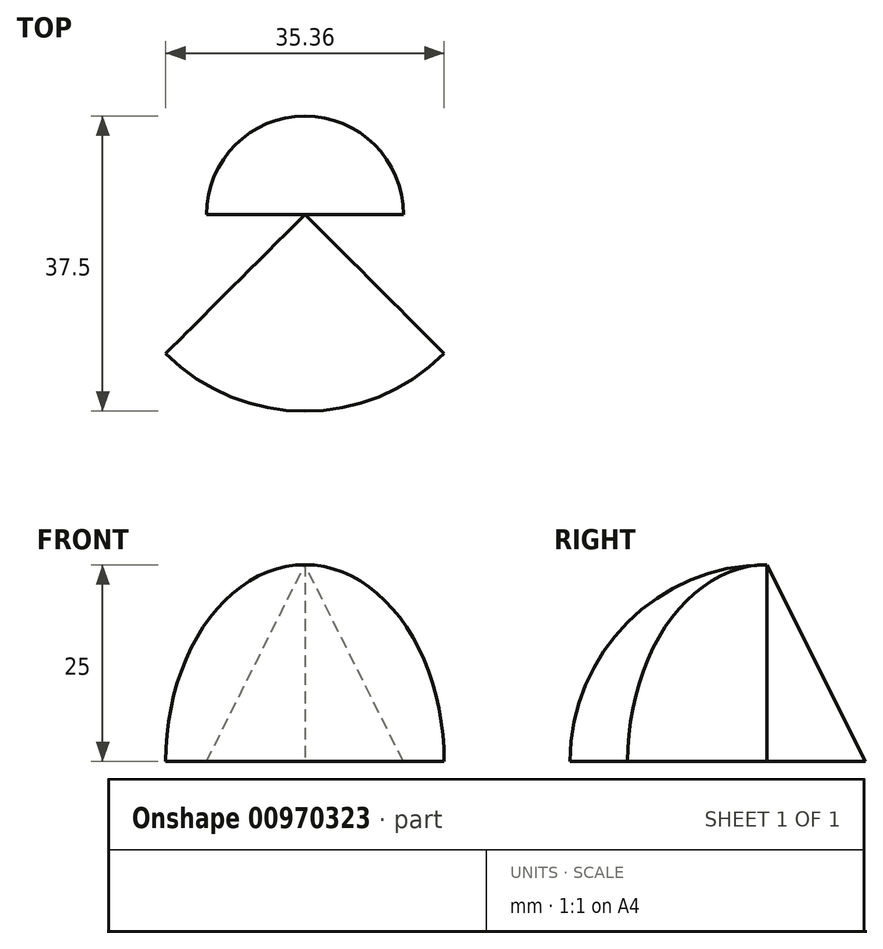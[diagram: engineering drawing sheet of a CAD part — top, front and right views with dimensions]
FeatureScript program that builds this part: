
annotation { "Feature Type Name" : "Feature", "Feature Type Description" : "" }
export const myFeature = defineFeature(function(context is Context, id is Id, definition is map)
    precondition{}
    {
        {
            var Q0;
            Q0=qCreatedBy(makeId("Front.planeOp"),FACE);
            var sketch = newSketch(context, id + "F0", { "sketchPlane" : qUnion([Q0])});
            skLineSegment(sketch, "E0", {"start": v(0, 0) * mm, "end": v(-12.5, 0) * mm});
            skLineSegment(sketch, "E1", {"start": v(-12.5, 0) * mm, "end": v(0, 25) * mm});
            skLineSegment(sketch, "E2", {"start": v(0, 25) * mm, "end": v(0, 0) * mm});
            skSolve(sketch);
        }
        {
            var Q0;
            Q0 = qSketchRegion(id + "F0", true);
            var Q1;
            Q1=sQuery(id+"F0.wireOp",EDGE,"E2");
            revolve(context, id + "F1", {"surfaceOperationType" : NewSurfaceOperationType.NEW, "entities" : qUnion([Q0]), "axis" : qUnion([Q1]), "revolveType" : RevolveType.ONE_DIRECTION, "angle" : 180 * degree});
        }
        {
            var Q0;
            Q0=qCreatedBy(makeId("Right.planeOp"),FACE);
            var sketch = newSketch(context, id + "F2", { "sketchPlane" : qUnion([Q0])});
            skArc(sketch, "E3", {"start": v(0, 25) * mm, "mid": v(-17.68, 17.68) * mm, "end": v(-25, 0) * mm});
            skLineSegment(sketch, "E4", {"start": v(0, 25) * mm, "end": v(0, 0) * mm});
            skLineSegment(sketch, "E5", {"start": v(-25, 0) * mm, "end": v(0, 0) * mm});
            skSolve(sketch);
        }
        {
            var Q0;
            Q0=makeQuery(id+"F2.imprint","IMPRINT",FACE,{"disambiguationData":[TD([[makeQuery(id+"F2.imprint","IMPRINT",EDGE,{"derivedFrom":sQuery(id+"F2.wireOp",EDGE,"E3")}),1.0]])]});
            var Q1;
            Q1=sQuery(id+"F2.wireOp",EDGE,"E4");
            revolve(context, id + "F3", {"surfaceOperationType" : NewSurfaceOperationType.NEW, "entities" : qUnion([Q0]), "axis" : qUnion([Q1]), "revolveType" : RevolveType.SYMMETRIC, "angle" : 90 * degree});
        }
    });
